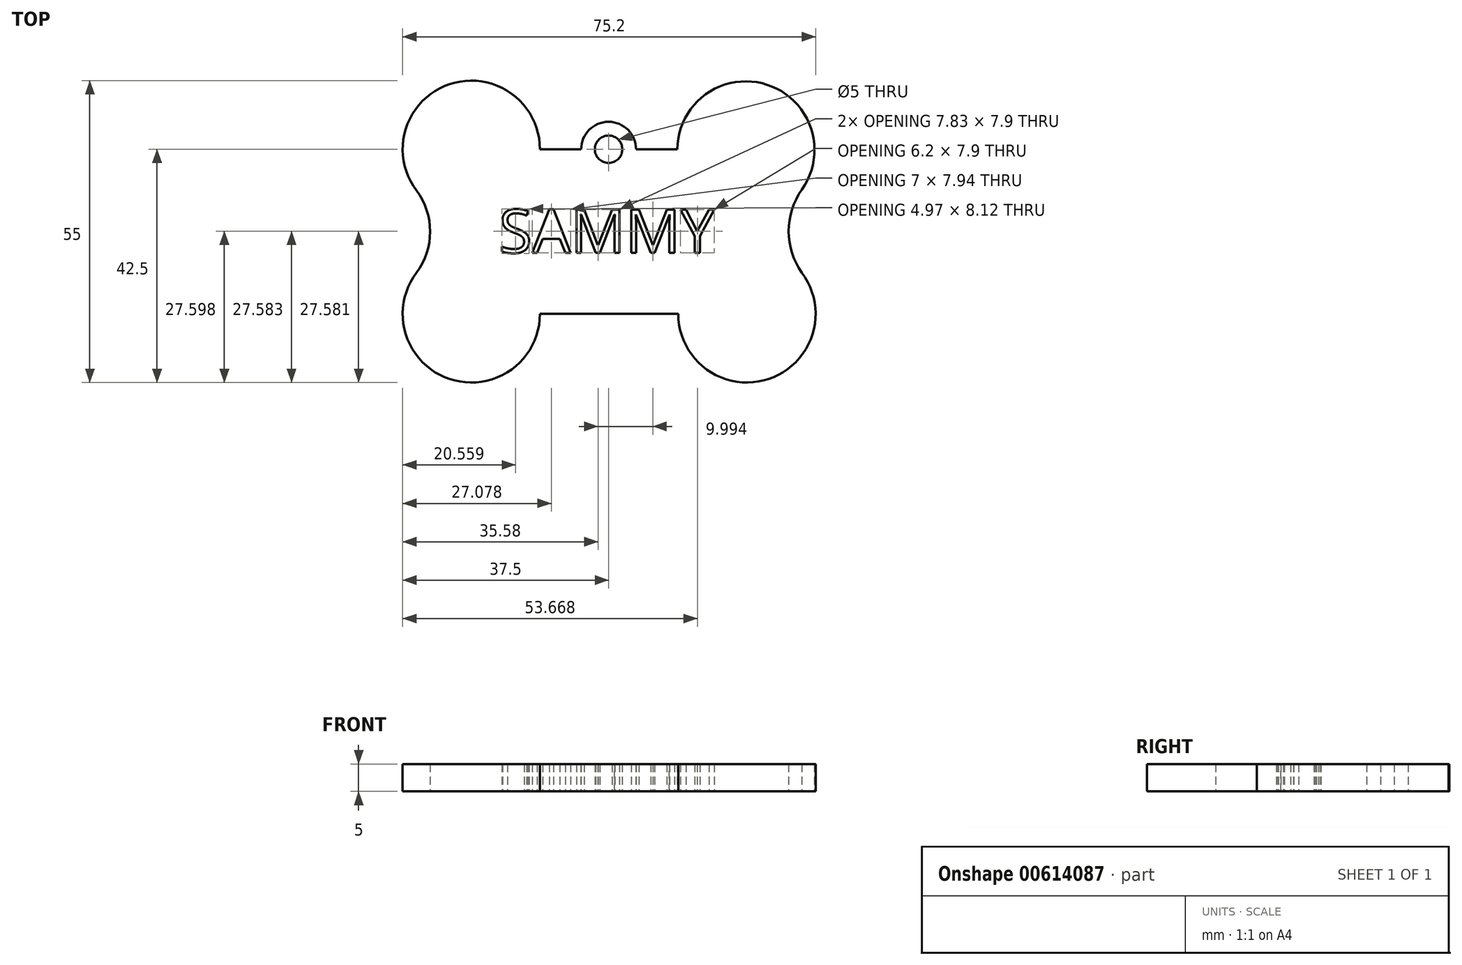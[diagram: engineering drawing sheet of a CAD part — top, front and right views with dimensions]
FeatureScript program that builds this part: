
annotation { "Feature Type Name" : "Feature", "Feature Type Description" : "" }
export const myFeature = defineFeature(function(context is Context, id is Id, definition is map)
    precondition{}
    {
        {
            var Q0;
            Q0=qCreatedBy(makeId("Top.planeOp"),FACE);
            var sketch = newSketch(context, id + "F0", { "sketchPlane" : qUnion([Q0])});
            skPoint(sketch, "E0.middle", {"position": v(0, 0) * mm});
            skArc(sketch, "E1", {"start": v(-12.5, 15) * mm, "mid": v(-28.95, 26.86) * mm, "end": v(-35, 7.5) * mm});
            skArc(sketch, "E2", {"start": v(-35, -7.5) * mm, "mid": v(-28.95, -26.86) * mm, "end": v(-12.5, -15) * mm});
            skArc(sketch, "E3", {"start": v(35.2, 7.64) * mm, "mid": v(28.85, 26.76) * mm, "end": v(12.5, 15) * mm});
            skArc(sketch, "E4", {"start": v(12.7, -15) * mm, "mid": v(29.15, -26.86) * mm, "end": v(35.2, -7.5) * mm});
            skPoint(sketch, "E5.orphan", {"position": v(-30, 15) * mm});
            skLineSegment(sketch, "E6.trimOffspring", {"start": v(12.5, 15) * mm, "end": v(5, 15) * mm});
            skPoint(sketch, "E0.top.start.orphan", {"position": v(30, 15) * mm});
            skLineSegment(sketch, "E7.trimOffspring", {"start": v(12.7, -15) * mm, "end": v(-12.5, -15) * mm});
            skPoint(sketch, "E8.start.orphan", {"position": v(-30, -15) * mm});
            skPoint(sketch, "E0.bottom.start.orphan", {"position": v(30, -15) * mm});
            skText(sketch, "E9", { "text": "SAMMY", "fontName": "OpenSans-Regular.ttf"});
            skArc(sketch, "E10", {"start": v(-35, 7.5) * mm, "mid": v(-32.5, 0) * mm, "end": v(-35, -7.5) * mm});
            skArc(sketch, "E11", {"start": v(35.2, 7.64) * mm, "mid": v(32.78, 0.07) * mm, "end": v(35.2, -7.5) * mm});
            skArc(sketch, "E12", {"start": v(5, 15) * mm, "mid": v(0, 20) * mm, "end": v(-5, 15) * mm});
            skLineSegment(sketch, "E13.trimOffspring", {"start": v(-5, 15) * mm, "end": v(-12.5, 15) * mm});
            skCircle(sketch, "E14", {"center": v(0, 15) * mm, "radius": 2.5 * mm});
            const initialGuessF0  = {"E9": [-0.02, -0.00387, 1, 0, 0.00797]};
            skSetInitialGuess(sketch, initialGuessF0);
            skSolve(sketch);
        }
        {
            var Q0;
            Q0=makeQuery(id+"F0.imprint","IMPRINT",FACE,{"disambiguationData":[TD([[makeQuery(id+"F0.imprint","IMPRINT",EDGE,{"derivedFrom":sQuery(id+"F0.wireOp",EDGE,"E1")}),1.0]])]});
            extrude(context, id + "F1", {"entities" : qUnion([Q0]), "depth" : 5 * mm, "offsetDistance" : 25 * mm});
        }
    });
